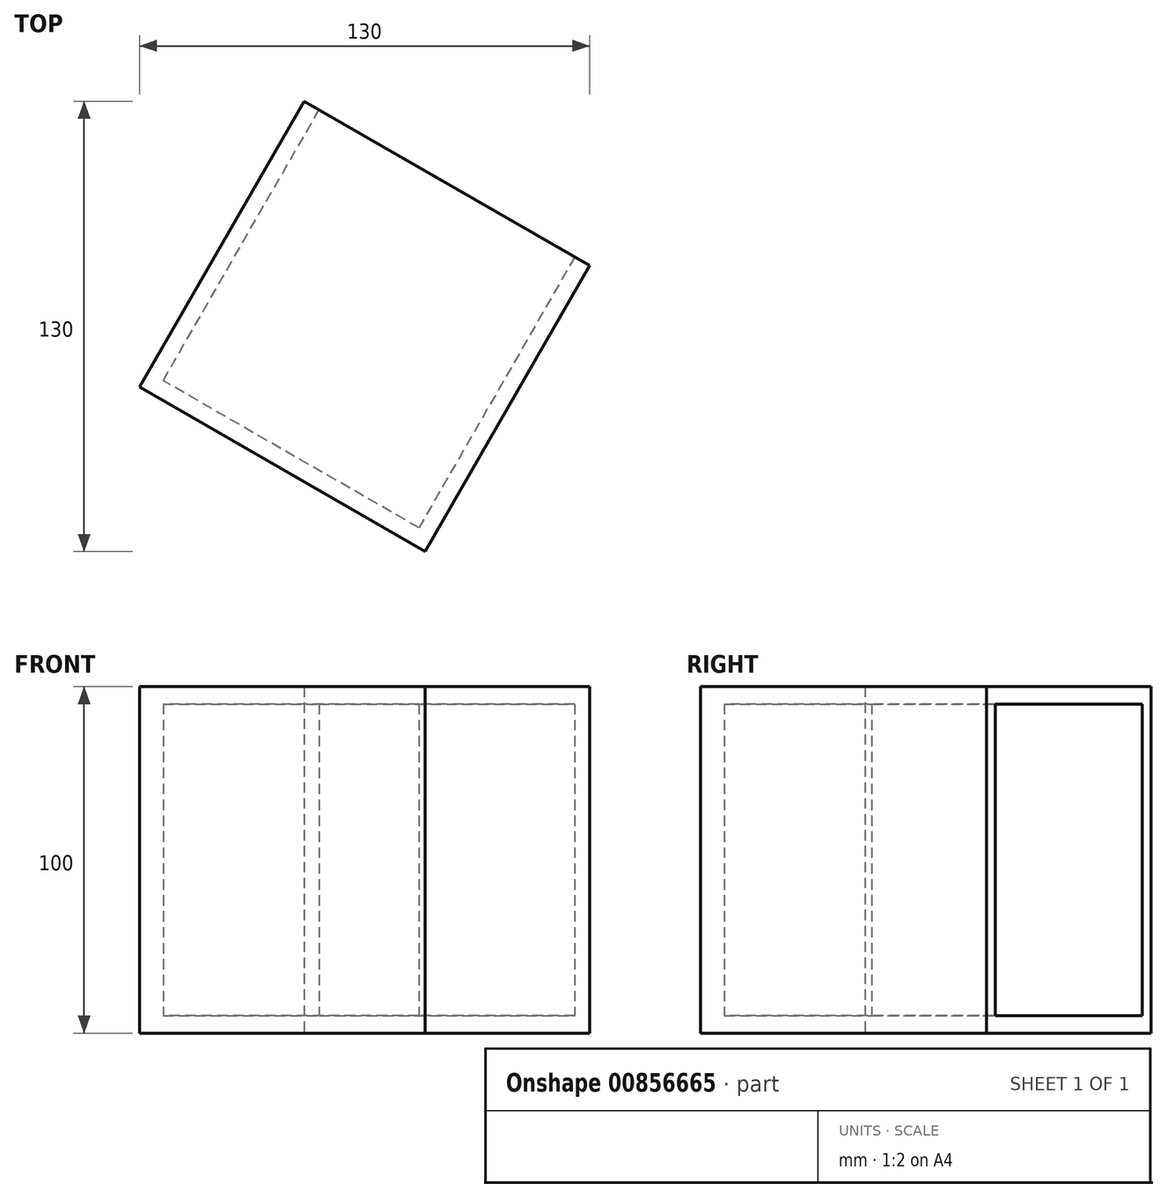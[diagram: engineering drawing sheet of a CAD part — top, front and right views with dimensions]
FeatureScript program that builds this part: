
annotation { "Feature Type Name" : "Feature", "Feature Type Description" : "" }
export const myFeature = defineFeature(function(context is Context, id is Id, definition is map)
    precondition{}
    {
        {
            var Q0;
            Q0=qCreatedBy(makeId("Top.planeOp"),FACE);
            var sketch = newSketch(context, id + "F0", { "sketchPlane" : qUnion([Q0])});
            skCircle(sketch, "E0.cCircle", {"center": v(0, 0) * mm, "radius": 47.6 * mm, "construction": true});
            skLineSegment(sketch, "E0.0", {"start": v(-17.51, 65) * mm, "end": v(65, 17.51) * mm});
            skLineSegment(sketch, "E0.1", {"start": v(65, 17.51) * mm, "end": v(17.51, -65) * mm});
            skLineSegment(sketch, "E0.2", {"start": v(17.51, -65) * mm, "end": v(-65, -17.51) * mm});
            skLineSegment(sketch, "E0.3", {"start": v(-65, -17.51) * mm, "end": v(-17.51, 65) * mm});
            skPoint(sketch, "E0.0.midPoint", {"position": v(23.74, 41.25) * mm});
            skSolve(sketch);
        }
        {
            var Q0;
            Q0=makeQuery(id+"F0.imprint","IMPRINT",FACE,{"disambiguationData":[TD([[makeQuery(id+"F0.imprint","IMPRINT",EDGE,{"derivedFrom":sQuery(id+"F0.wireOp",EDGE,"E0.0")}),-1.0]])]});
            extrude(context, id + "F1", {"entities" : qUnion([Q0]), "depth" : 100 * mm, "offsetDistance" : 25 * mm});
        }
        {
            var Q0;
            Q0=makeQuery(id+"F1.opExtrude","SWEPT_FACE",FACE,{"disambiguationData":[OSD([sQuery(id+"F0.wireOp",EDGE,"E0.0")])]});
            shell(context, id + "F2", {"entities" : qUnion([Q0]), "thickness" : 5 * mm});
        }
    });
